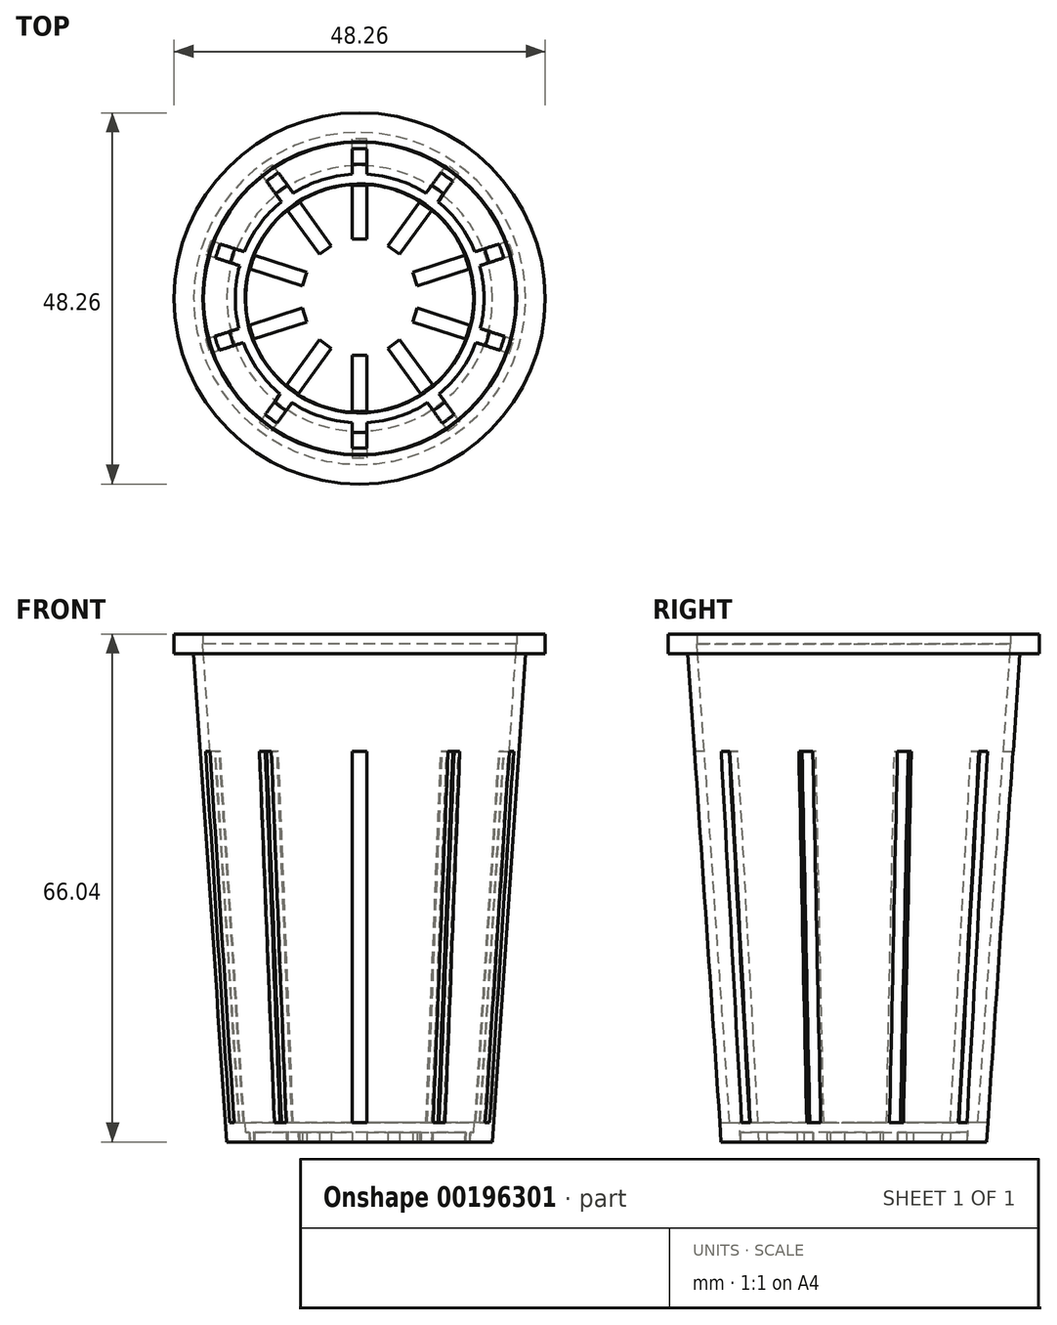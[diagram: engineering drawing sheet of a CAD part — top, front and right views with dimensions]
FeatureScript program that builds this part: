
annotation { "Feature Type Name" : "Feature", "Feature Type Description" : "" }
export const myFeature = defineFeature(function(context is Context, id is Id, definition is map)
    precondition{}
    {
        {
            var Q0;
            Q0=qCreatedBy(makeId("Front.planeOp"),FACE);
            var sketch = newSketch(context, id + "F0", { "sketchPlane" : qUnion([Q0])});
            skLineSegment(sketch, "E0", {"start": v(0, 0) * mm, "end": v(0, 63.5) * mm});
            skLineSegment(sketch, "E1", {"start": v(0, 63.5) * mm, "end": v(0, 66.04) * mm});
            skLineSegment(sketch, "E2", {"start": v(0, 66.04) * mm, "end": v(24.13, 66.04) * mm});
            skLineSegment(sketch, "E3", {"start": v(24.13, 66.04) * mm, "end": v(24.13, 63.5) * mm});
            skLineSegment(sketch, "E4", {"start": v(24.13, 63.5) * mm, "end": v(0, 63.5) * mm});
            skLineSegment(sketch, "E5", {"start": v(0, 63.5) * mm, "end": v(21.59, 63.5) * mm});
            skLineSegment(sketch, "E6", {"start": v(0, 0) * mm, "end": v(17.27, 0) * mm});
            skLineSegment(sketch, "E7", {"start": v(17.27, 0) * mm, "end": v(21.59, 63.5) * mm});
            skSolve(sketch);
        }
        {
            var Q0;
            Q0=qSketchRegion(id+"F0",true);
            var Q1;
            Q1=sQuery(id+"F0.wireOp",EDGE,"E0");
            revolve(context, id + "F1", {"entities" : qUnion([Q0]), "axis" : qUnion([Q1]), "revolveType" : RevolveType.FULL});
        }
        {
            var Q0;
            Q0=makeQuery(id+"F1.opRevolve","SWEPT_FACE",FACE,{"disambiguationData":[OSD([sQuery(id+"F0.wireOp",EDGE,"E2")])]});
            shell(context, id + "F2", {"entities" : qUnion([Q0]), "thickness" : 1.27 * mm});
        }
        {
            var Q0;
            Q0=makeQuery(id+"F2.opShell","OFFSET_FACE",FACE,{"disambiguationData":[OSD([sQuery(id+"F0.wireOp",EDGE,"E4")])]});
            extrude(context, id + "F3", {"entities" : qUnion([Q0]), "operationType" : NewBodyOperationType.ADD, "depth" : 1.27 * mm});
        }
        {
            var Q0;
            Q0=qCreatedBy(makeId("Top.planeOp"),FACE);
            cPlane(context, id + "F4", {"entities" : qUnion([Q0]), "cplaneType" : CPlaneType.OFFSET, "offset" : 63.5 * mm, "width" : 152.4 * mm, "height" : 152.4 * mm});
        }
        {
            var Q0;
            Q0=qCreatedBy(id+"F4.planeOp",FACE);
            var sketch = newSketch(context, id + "F5", { "sketchPlane" : qUnion([Q0])});
            skCircle(sketch, "E8", {"center": v(0, 0) * mm, "radius": 20.32 * mm});
            skSolve(sketch);
        }
        {
            var Q0;
            Q0=qSketchRegion(id+"F5",true);
            extrude(context, id + "F6", {"entities" : qUnion([Q0]), "operationType" : NewBodyOperationType.REMOVE, "depth" : 25.4 * mm});
        }
        {
            var Q0;
            Q0=qCreatedBy(makeId("Top.planeOp"),FACE);
            var sketch = newSketch(context, id + "F7", { "sketchPlane" : qUnion([Q0])});
            skLineSegment(sketch, "E9", {"start": v(0, 0) * mm, "end": v(0, -17.27) * mm});
            skLineSegment(sketch, "E10.bottom", {"start": v(0.95, -7.37) * mm, "end": v(-0.95, -7.37) * mm});
            skLineSegment(sketch, "E10.top", {"start": v(0.95, -27.18) * mm, "end": v(-0.95, -27.18) * mm});
            skLineSegment(sketch, "E10.left", {"start": v(0.95, -7.37) * mm, "end": v(0.95, -27.18) * mm});
            skLineSegment(sketch, "E10.right", {"start": v(-0.95, -7.37) * mm, "end": v(-0.95, -27.18) * mm});
            skPoint(sketch, "E10.middle", {"position": v(0, -17.27) * mm});
            skLineSegment(sketch, "E11.1.0", {"start": v(3.67, -6.48) * mm, "end": v(15.31, -22.51) * mm});
            skLineSegment(sketch, "E11.1.1", {"start": v(5.2, -5.36) * mm, "end": v(16.85, -21.4) * mm});
            skLineSegment(sketch, "E11.1.2", {"start": v(5.2, -5.36) * mm, "end": v(3.67, -6.48) * mm});
            skLineSegment(sketch, "E11.1.3", {"start": v(16.85, -21.4) * mm, "end": v(15.31, -22.51) * mm});
            skLineSegment(sketch, "E11.2.0", {"start": v(6.88, -3.06) * mm, "end": v(25.73, -9.18) * mm});
            skLineSegment(sketch, "E11.2.1", {"start": v(7.47, -1.24) * mm, "end": v(26.31, -7.37) * mm});
            skLineSegment(sketch, "E11.2.2", {"start": v(7.47, -1.24) * mm, "end": v(6.88, -3.06) * mm});
            skLineSegment(sketch, "E11.2.3", {"start": v(26.31, -7.37) * mm, "end": v(25.73, -9.18) * mm});
            skLineSegment(sketch, "E11.3.0", {"start": v(7.47, 1.6) * mm, "end": v(26.31, 7.73) * mm});
            skLineSegment(sketch, "E11.3.1", {"start": v(6.88, 3.42) * mm, "end": v(25.73, 9.54) * mm});
            skLineSegment(sketch, "E11.3.2", {"start": v(6.88, 3.42) * mm, "end": v(7.47, 1.6) * mm});
            skLineSegment(sketch, "E11.3.3", {"start": v(25.73, 9.54) * mm, "end": v(26.31, 7.73) * mm});
            skLineSegment(sketch, "E11.4.0", {"start": v(5.2, 5.73) * mm, "end": v(16.85, 21.76) * mm});
            skLineSegment(sketch, "E11.4.1", {"start": v(3.67, 6.85) * mm, "end": v(15.31, 22.88) * mm});
            skLineSegment(sketch, "E11.4.2", {"start": v(3.67, 6.85) * mm, "end": v(5.2, 5.73) * mm});
            skLineSegment(sketch, "E11.4.3", {"start": v(15.31, 22.88) * mm, "end": v(16.85, 21.76) * mm});
            skLineSegment(sketch, "E11.5.0", {"start": v(0.95, 7.73) * mm, "end": v(0.95, 27.54) * mm});
            skLineSegment(sketch, "E11.5.1", {"start": v(-0.95, 7.73) * mm, "end": v(-0.95, 27.54) * mm});
            skLineSegment(sketch, "E11.5.2", {"start": v(-0.95, 7.73) * mm, "end": v(0.95, 7.73) * mm});
            skLineSegment(sketch, "E11.5.3", {"start": v(-0.95, 27.54) * mm, "end": v(0.95, 27.54) * mm});
            skLineSegment(sketch, "E11.6.0", {"start": v(-3.67, 6.85) * mm, "end": v(-15.31, 22.88) * mm});
            skLineSegment(sketch, "E11.6.1", {"start": v(-5.2, 5.73) * mm, "end": v(-16.85, 21.76) * mm});
            skLineSegment(sketch, "E11.6.2", {"start": v(-5.2, 5.73) * mm, "end": v(-3.67, 6.85) * mm});
            skLineSegment(sketch, "E11.6.3", {"start": v(-16.85, 21.76) * mm, "end": v(-15.31, 22.88) * mm});
            skLineSegment(sketch, "E11.7.0", {"start": v(-6.88, 3.42) * mm, "end": v(-25.73, 9.54) * mm});
            skLineSegment(sketch, "E11.7.1", {"start": v(-7.47, 1.6) * mm, "end": v(-26.31, 7.73) * mm});
            skLineSegment(sketch, "E11.7.2", {"start": v(-7.47, 1.6) * mm, "end": v(-6.88, 3.42) * mm});
            skLineSegment(sketch, "E11.7.3", {"start": v(-26.31, 7.73) * mm, "end": v(-25.73, 9.54) * mm});
            skLineSegment(sketch, "E11.8.0", {"start": v(-7.47, -1.24) * mm, "end": v(-26.31, -7.37) * mm});
            skLineSegment(sketch, "E11.8.1", {"start": v(-6.88, -3.06) * mm, "end": v(-25.73, -9.18) * mm});
            skLineSegment(sketch, "E11.8.2", {"start": v(-6.88, -3.06) * mm, "end": v(-7.47, -1.24) * mm});
            skLineSegment(sketch, "E11.8.3", {"start": v(-25.73, -9.18) * mm, "end": v(-26.31, -7.37) * mm});
            skLineSegment(sketch, "E11.9.0", {"start": v(-5.2, -5.36) * mm, "end": v(-16.85, -21.4) * mm});
            skLineSegment(sketch, "E11.9.1", {"start": v(-3.67, -6.48) * mm, "end": v(-15.31, -22.51) * mm});
            skLineSegment(sketch, "E11.9.2", {"start": v(-3.67, -6.48) * mm, "end": v(-5.2, -5.36) * mm});
            skLineSegment(sketch, "E11.9.3", {"start": v(-15.31, -22.51) * mm, "end": v(-16.85, -21.4) * mm});
            skPoint(sketch, "E11.center", {"position": v(0, 0.18) * mm});
            skSolve(sketch);
        }
        {
            var Q0;
            Q0=qSketchRegion(id+"F7",true);
            extrude(context, id + "F8", {"entities" : qUnion([Q0]), "operationType" : NewBodyOperationType.REMOVE, "depth" : 50.8 * mm});
        }
        {
            var Q0;
            Q0=qCreatedBy(makeId("Front.planeOp"),FACE);
            var sketch = newSketch(context, id + "F9", { "sketchPlane" : qUnion([Q0])});
            skLineSegment(sketch, "E12", {"start": v(0, 0) * mm, "end": v(17.27, 0) * mm});
            skLineSegment(sketch, "E13", {"start": v(0, 0) * mm, "end": v(0, 2.54) * mm});
            skLineSegment(sketch, "E14", {"start": v(0, 2.54) * mm, "end": v(17.44, 2.54) * mm});
            skLineSegment(sketch, "E15", {"start": v(17.44, 2.54) * mm, "end": v(17.27, 0) * mm});
            skLineSegment(sketch, "E16", {"start": v(17.27, 0) * mm, "end": v(14.73, 0) * mm});
            skLineSegment(sketch, "E17", {"start": v(14.73, 0) * mm, "end": v(14.9, 2.54) * mm});
            skSolve(sketch);
        }
        {
            var Q0;
            {var subQ0=sQuery(id+"F9.wireOp",EDGE,"E15");Q0=makeQuery(id+"F9.imprint","IMPRINT",FACE,{"disambiguationData":[TD([[makeQuery(id+"F9.imprint","IMPRINT",EDGE,{"derivedFrom":subQ0}),-1.0]])]});}
            var Q1;
            Q1=sQuery(id+"F9.wireOp",EDGE,"E13");
            revolve(context, id + "F10", {"operationType" : NewBodyOperationType.ADD, "entities" : qUnion([Q0]), "axis" : qUnion([Q1]), "revolveType" : RevolveType.FULL});
        }
    });
